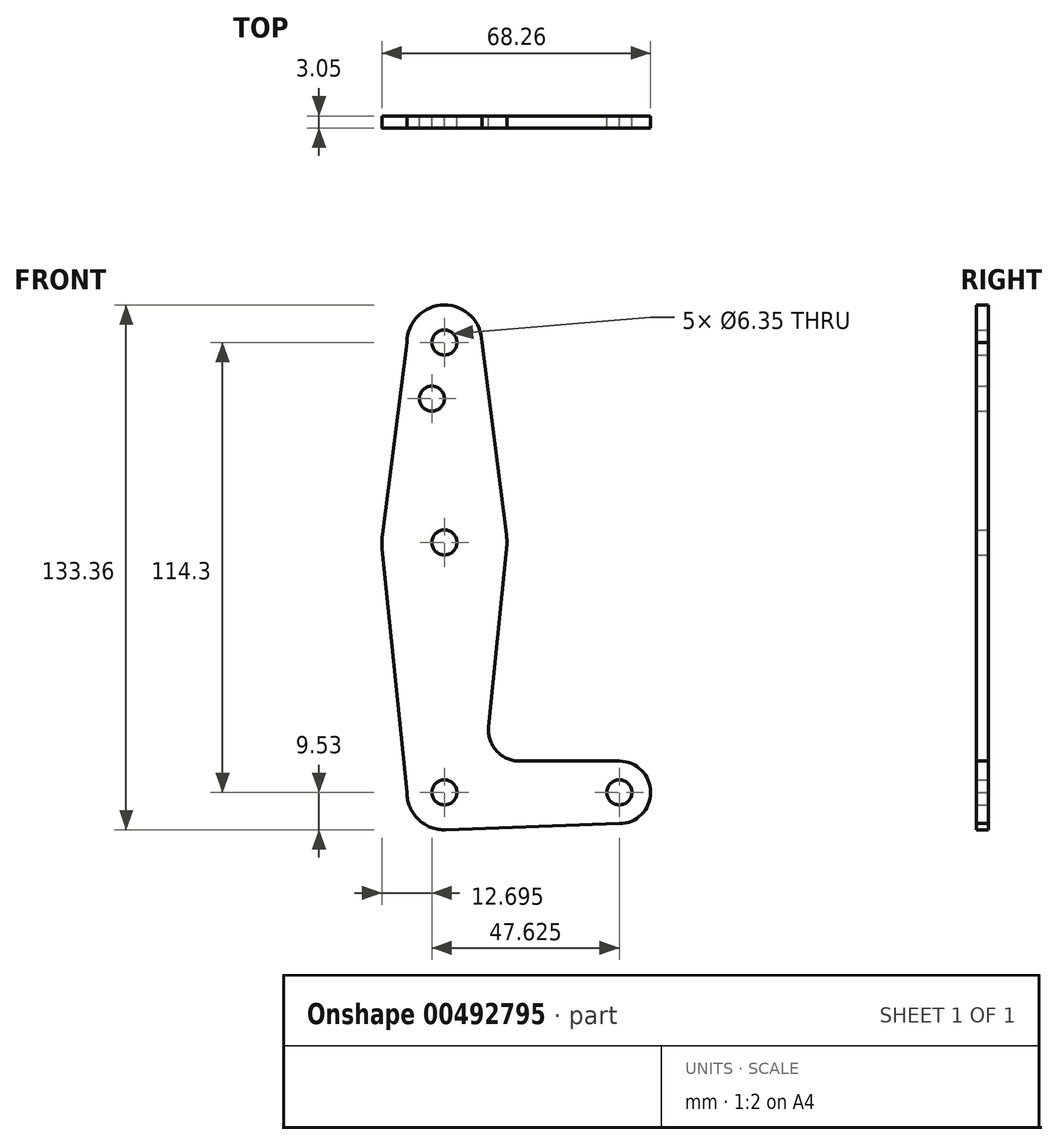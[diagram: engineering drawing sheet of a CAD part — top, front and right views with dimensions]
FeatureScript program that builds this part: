
annotation { "Feature Type Name" : "Feature", "Feature Type Description" : "" }
export const myFeature = defineFeature(function(context is Context, id is Id, definition is map)
    precondition{}
    {
        {
            var Q0;
            Q0=qCreatedBy(makeId("Front.planeOp"),FACE);
            var sketch = newSketch(context, id + "F0", { "sketchPlane" : qUnion([Q0])});
            skLineSegment(sketch, "E0", {"start": v(0, 0) * mm, "end": v(44.45, 0) * mm, "construction": true});
            skCircle(sketch, "E1", {"center": v(0, 0) * mm, "radius": 9.53 * mm});
            skCircle(sketch, "E2", {"center": v(44.45, 0) * mm, "radius": 7.94 * mm});
            skLineSegment(sketch, "E3", {"start": v(44.45, -7.94) * mm, "end": v(0, -9.53) * mm});
            skLineSegment(sketch, "E4", {"start": v(0, -9.53) * mm, "end": v(44.45, -7.94) * mm});
            skLineSegment(sketch, "E5", {"start": v(0, 9.52) * mm, "end": v(0, 114.3) * mm, "construction": true});
            skCircle(sketch, "E6", {"center": v(0, 114.3) * mm, "radius": 9.53 * mm});
            skCircle(sketch, "E7", {"center": v(0, 63.5) * mm, "radius": 15.88 * mm});
            skLineSegment(sketch, "E8", {"start": v(-9.53, 114.3) * mm, "end": v(-15.75, 65.5) * mm});
            skLineSegment(sketch, "E9", {"start": v(9.52, 114.3) * mm, "end": v(15.75, 65.5) * mm});
            skLineSegment(sketch, "E10", {"start": v(-9.53, 0) * mm, "end": v(-15.8, 61.9) * mm});
            skLineSegment(sketch, "E11", {"start": v(11.22, 16.69) * mm, "end": v(15.8, 61.9) * mm});
            skLineSegment(sketch, "E12", {"start": v(19.12, 7.94) * mm, "end": v(44.45, 7.94) * mm});
            skCircle(sketch, "E13", {"center": v(0, 114.3) * mm, "radius": 3.18 * mm});
            skCircle(sketch, "E14", {"center": v(0, 63.5) * mm, "radius": 3.18 * mm});
            skCircle(sketch, "E15", {"center": v(0, 0) * mm, "radius": 3.18 * mm});
            skCircle(sketch, "E16", {"center": v(44.45, 0) * mm, "radius": 3.18 * mm});
            skCircle(sketch, "E17", {"center": v(-3.18, 100.03) * mm, "radius": 3.18 * mm});
            skArc(sketch, "E18.filletArc", {"start": v(11.22, 16.69) * mm, "mid": v(13.23, 10.56) * mm, "end": v(19.12, 7.94) * mm});
            skSolve(sketch);
        }
        {
            var Q0;
            Q0 = qSketchRegion(id + "F0", true);
            extrude(context, id + "F1", {"entities" : qUnion([Q0]), "depth" : 3.05 * mm});
        }
    });
